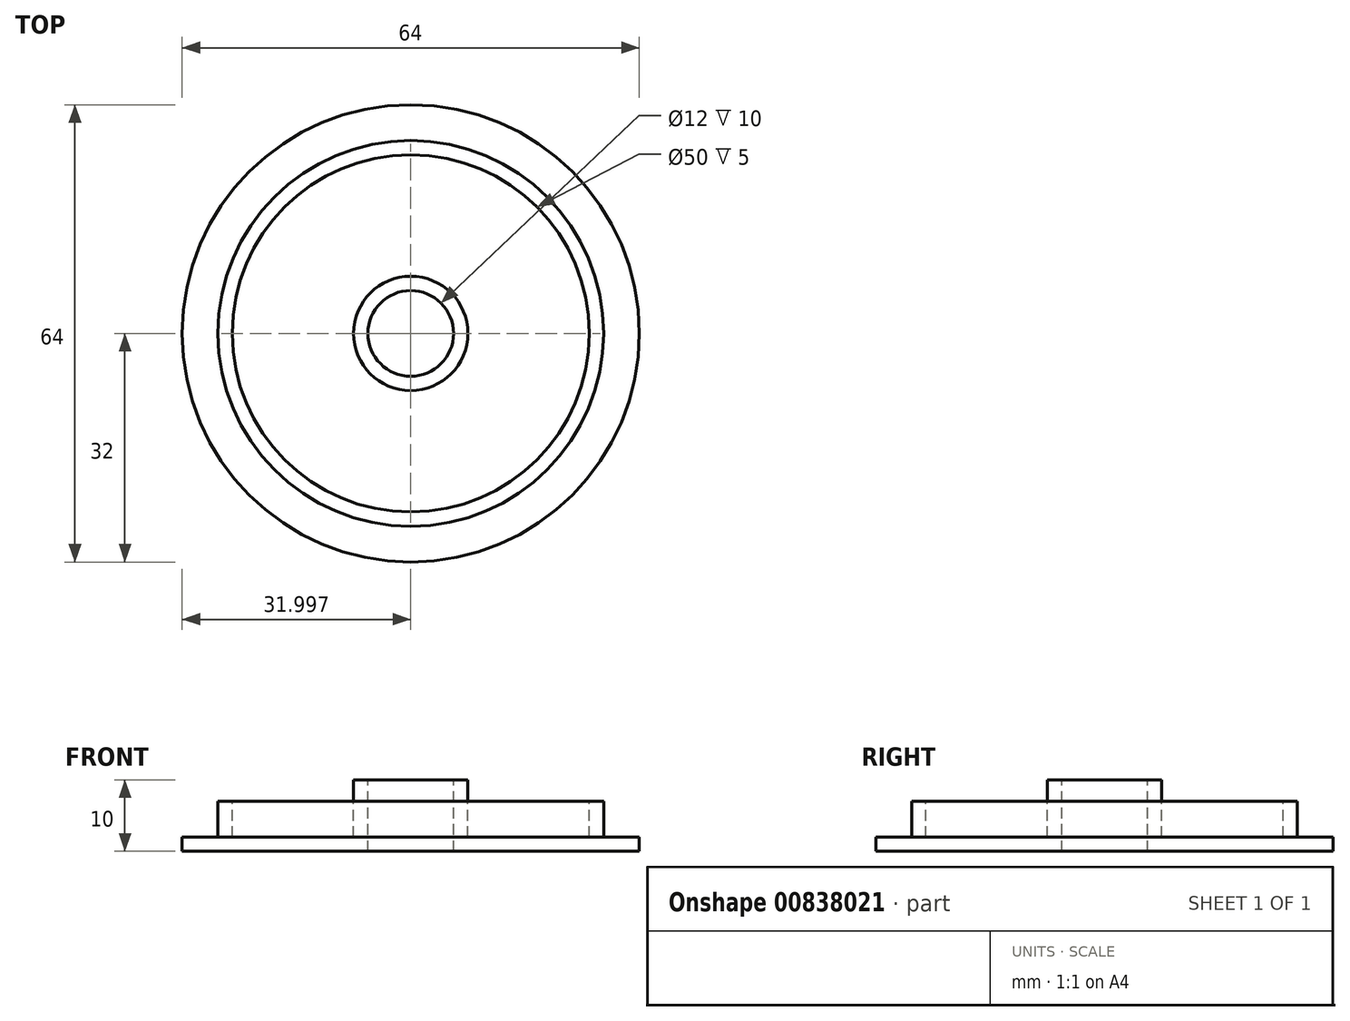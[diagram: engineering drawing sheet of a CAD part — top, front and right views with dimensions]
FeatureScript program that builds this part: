
annotation { "Feature Type Name" : "Feature", "Feature Type Description" : "" }
export const myFeature = defineFeature(function(context is Context, id is Id, definition is map)
    precondition{}
    {
        {
            var Q0;
            Q0=qCreatedBy(makeId("Front.planeOp"),FACE);
            var sketch = newSketch(context, id + "F0", { "sketchPlane" : qUnion([Q0])});
            skLineSegment(sketch, "E0", {"start": v(-21.91, 24.59) * mm, "end": v(-21.91, 19.75) * mm});
            skLineSegment(sketch, "E1", {"start": v(-27.91, 30.5) * mm, "end": v(-27.91, 20.5) * mm});
            skLineSegment(sketch, "E2", {"start": v(-27.91, 20.5) * mm, "end": v(-53.91, 20.5) * mm});
            skLineSegment(sketch, "E3", {"start": v(-53.91, 20.5) * mm, "end": v(-53.91, 22.5) * mm});
            skLineSegment(sketch, "E4", {"start": v(-53.91, 22.5) * mm, "end": v(-48.91, 22.5) * mm});
            skLineSegment(sketch, "E5", {"start": v(-48.91, 22.5) * mm, "end": v(-48.91, 27.5) * mm});
            skLineSegment(sketch, "E6", {"start": v(-48.91, 27.5) * mm, "end": v(-46.91, 27.5) * mm});
            skLineSegment(sketch, "E7", {"start": v(-46.91, 27.5) * mm, "end": v(-46.91, 22.5) * mm});
            skLineSegment(sketch, "E8", {"start": v(-46.91, 22.5) * mm, "end": v(-29.91, 22.5) * mm});
            skLineSegment(sketch, "E9", {"start": v(-29.91, 22.5) * mm, "end": v(-29.91, 30.5) * mm});
            skLineSegment(sketch, "E10", {"start": v(-29.91, 30.5) * mm, "end": v(-27.91, 30.5) * mm});
            skSolve(sketch);
        }
        {
            var Q0;
            Q0 = qSketchRegion(id + "F0", true);
            var Q1;
            Q1=sQuery(id+"F0.wireOp",EDGE,"E0");
            revolve(context, id + "F1", {"surfaceOperationType" : NewSurfaceOperationType.NEW, "entities" : qUnion([Q0]), "axis" : qUnion([Q1]), "revolveType" : RevolveType.FULL});
        }
    });
